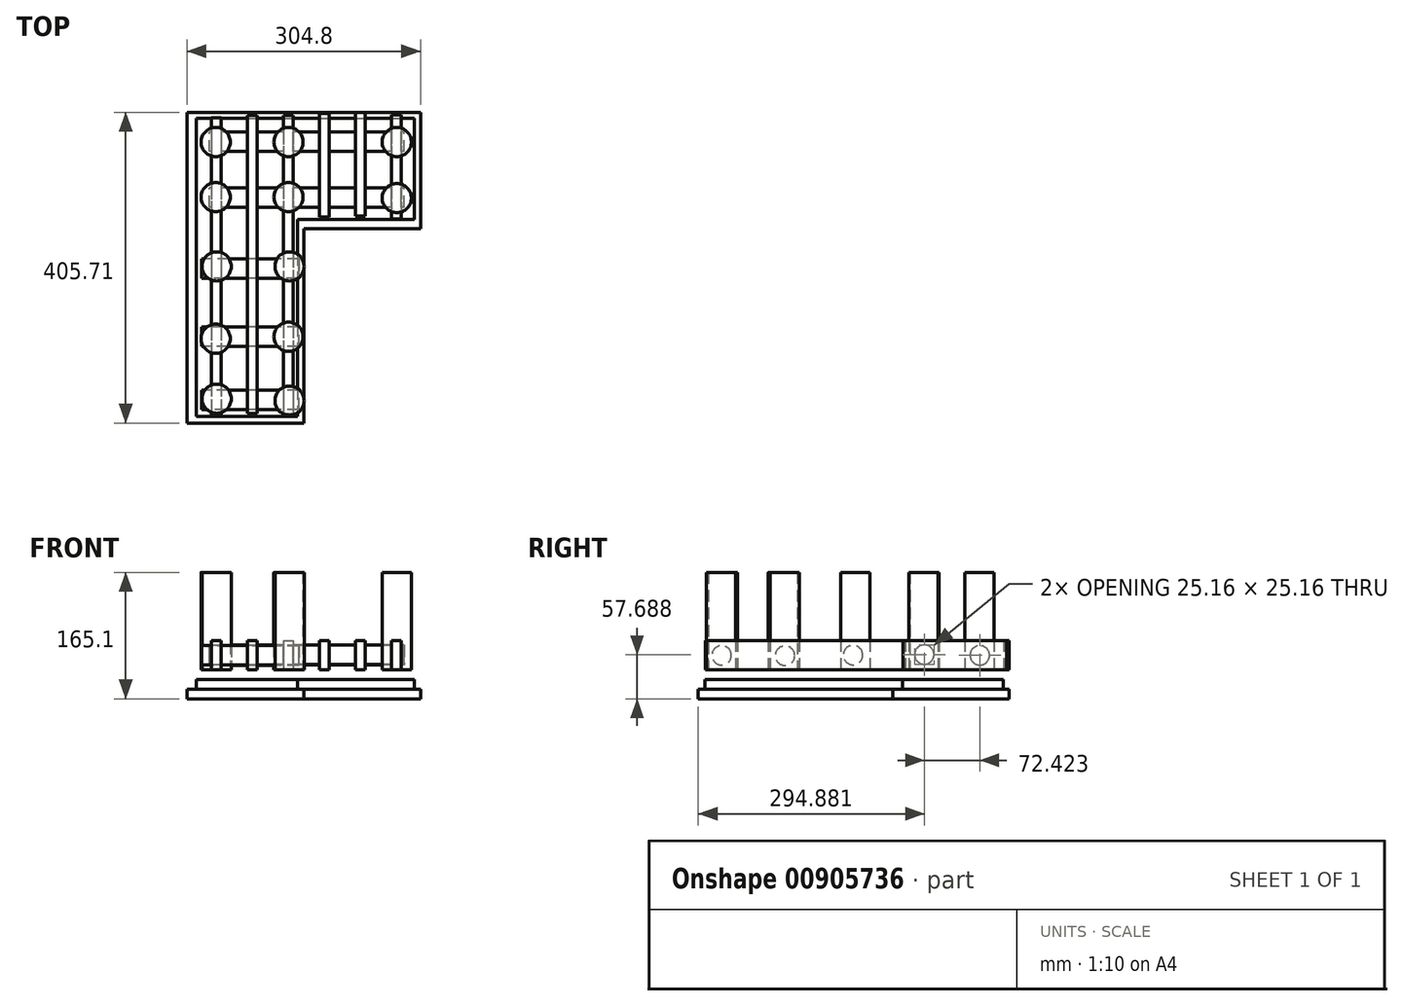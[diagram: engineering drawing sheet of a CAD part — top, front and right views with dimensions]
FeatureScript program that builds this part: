
annotation { "Feature Type Name" : "Feature", "Feature Type Description" : "" }
export const myFeature = defineFeature(function(context is Context, id is Id, definition is map)
    precondition{}
    {
        {
            var Q0;
            Q0=qCreatedBy(makeId("Top.planeOp"),FACE);
            var sketch = newSketch(context, id + "F0", { "sketchPlane" : qUnion([Q0])});
            skLineSegment(sketch, "E0.bottom", {"start": v(-152.4, 201.86) * mm, "end": v(152.4, 201.86) * mm});
            skLineSegment(sketch, "E0.top", {"start": v(-152.4, 201.06) * mm, "end": v(152.4, 201.06) * mm});
            skLineSegment(sketch, "E0.left", {"start": v(-152.4, 201.86) * mm, "end": v(-152.4, 201.06) * mm});
            skLineSegment(sketch, "E0.right", {"start": v(152.4, 201.86) * mm, "end": v(152.4, 201.06) * mm});
            skPoint(sketch, "E0.middle", {"position": v(0, 201.46) * mm});
            skLineSegment(sketch, "E1.bottom", {"start": v(-152.4, 201.86) * mm, "end": v(-152.4, 201.86) * mm});
            skLineSegment(sketch, "E1.top", {"start": v(-152.4, -204.54) * mm, "end": v(-152.4, -204.54) * mm});
            skLineSegment(sketch, "E1.left", {"start": v(-152.4, 201.86) * mm, "end": v(-152.4, -204.54) * mm});
            skLineSegment(sketch, "E1.right", {"start": v(-152.4, 201.86) * mm, "end": v(-152.4, -204.54) * mm});
            skLineSegment(sketch, "E2.bottom", {"start": v(-152.4, -204.54) * mm, "end": v(0, -204.54) * mm});
            skLineSegment(sketch, "E2.top", {"start": v(-152.4, -204.54) * mm, "end": v(0, -204.54) * mm});
            skLineSegment(sketch, "E2.right", {"start": v(0, -204.54) * mm, "end": v(0, -204.54) * mm});
            skLineSegment(sketch, "E3.top", {"start": v(0, 49.46) * mm, "end": v(0, 49.46) * mm});
            skLineSegment(sketch, "E3.left", {"start": v(0, -204.54) * mm, "end": v(0, 49.46) * mm});
            skLineSegment(sketch, "E3.right", {"start": v(0, -204.54) * mm, "end": v(0, 49.46) * mm});
            skLineSegment(sketch, "E4.bottom", {"start": v(0, 49.46) * mm, "end": v(152.4, 49.46) * mm});
            skLineSegment(sketch, "E4.top", {"start": v(0, 49.46) * mm, "end": v(152.4, 49.46) * mm});
            skLineSegment(sketch, "E4.right", {"start": v(152.4, 49.46) * mm, "end": v(152.4, 49.46) * mm});
            skLineSegment(sketch, "E5.bottom", {"start": v(152.4, 201.06) * mm, "end": v(152.4, 201.06) * mm});
            skLineSegment(sketch, "E5.left", {"start": v(152.4, 201.06) * mm, "end": v(152.4, 49.46) * mm});
            skLineSegment(sketch, "E5.right", {"start": v(152.4, 201.06) * mm, "end": v(152.4, 49.46) * mm});
            skSolve(sketch);
        }
        {
            var Q0;
            Q0=qCreatedBy(makeId("Top.planeOp"),FACE);
            var sketch = newSketch(context, id + "F1", { "sketchPlane" : qUnion([Q0])});
            skLineSegment(sketch, "E6.bottom", {"start": v(-148.7, 201.8) * mm, "end": v(-140.24, 201.8) * mm});
            skLineSegment(sketch, "E6.top", {"start": v(-148.7, -204.6) * mm, "end": v(-140.24, -204.6) * mm});
            skLineSegment(sketch, "E6.left", {"start": v(-148.7, 201.8) * mm, "end": v(-148.7, -204.6) * mm});
            skLineSegment(sketch, "E6.right", {"start": v(-140.24, 201.8) * mm, "end": v(-140.24, -204.6) * mm});
            skLineSegment(sketch, "E7.bottom", {"start": v(-140.24, 201.8) * mm, "end": v(156.1, 201.8) * mm});
            skLineSegment(sketch, "E7.top", {"start": v(-140.24, 193.33) * mm, "end": v(156.1, 193.33) * mm});
            skLineSegment(sketch, "E7.left", {"start": v(-140.24, 201.8) * mm, "end": v(-140.24, 193.33) * mm});
            skLineSegment(sketch, "E7.right", {"start": v(156.1, 201.8) * mm, "end": v(156.1, 193.33) * mm});
            skLineSegment(sketch, "E8.bottom", {"start": v(144.25, 193.33) * mm, "end": v(152.72, 193.33) * mm});
            skLineSegment(sketch, "E8.top", {"start": v(144.25, 49.4) * mm, "end": v(152.72, 49.4) * mm});
            skLineSegment(sketch, "E8.left", {"start": v(144.25, 193.33) * mm, "end": v(144.25, 49.4) * mm});
            skLineSegment(sketch, "E8.right", {"start": v(152.72, 193.33) * mm, "end": v(152.72, 49.4) * mm});
            skLineSegment(sketch, "E9.bottom", {"start": v(0, 53.12) * mm, "end": v(144.25, 53.12) * mm});
            skLineSegment(sketch, "E9.top", {"start": v(0, 61.58) * mm, "end": v(144.25, 61.58) * mm});
            skLineSegment(sketch, "E9.left", {"start": v(0, 53.12) * mm, "end": v(0, 61.58) * mm});
            skLineSegment(sketch, "E9.right", {"start": v(144.25, 53.12) * mm, "end": v(144.25, 61.58) * mm});
            skLineSegment(sketch, "E10.bottom", {"start": v(0, 61.58) * mm, "end": v(-8.47, 61.58) * mm});
            skLineSegment(sketch, "E10.top", {"start": v(0, -203.03) * mm, "end": v(-8.47, -203.03) * mm});
            skLineSegment(sketch, "E10.left", {"start": v(0, 61.58) * mm, "end": v(0, -203.03) * mm});
            skLineSegment(sketch, "E10.right", {"start": v(-8.47, 61.58) * mm, "end": v(-8.47, -203.03) * mm});
            skLineSegment(sketch, "E11.bottom", {"start": v(-140.24, -204.6) * mm, "end": v(-8.47, -204.6) * mm});
            skLineSegment(sketch, "E11.top", {"start": v(-140.24, -196.13) * mm, "end": v(-8.47, -196.13) * mm});
            skLineSegment(sketch, "E11.left", {"start": v(-140.24, -204.6) * mm, "end": v(-140.24, -196.13) * mm});
            skLineSegment(sketch, "E11.right", {"start": v(-8.47, -204.6) * mm, "end": v(-8.47, -196.13) * mm});
            skSolve(sketch);
        }
        {
            var Q0;
            Q0=makeQuery(id+"F0.imprint","IMPRINT",FACE,{"disambiguationData":[TD([[makeQuery(id+"F0.imprint","IMPRINT",EDGE,{"derivedFrom":sQuery(id+"F0.wireOp",EDGE,"E0.top")}),-1.0]])]});
            extrude(context, id + "F2", {"entities" : qUnion([Q0]), "depth" : 12.7 * mm, "offsetDistance" : 25.4 * mm});
        }
        {
            var Q0;
            {var subQ0=sQuery(id+"F1.wireOp",EDGE,"E9.top");Q0=makeQuery(id+"F1.imprint","IMPRINT",FACE,{"disambiguationData":[TD([[makeQuery(id+"F1.imprint","IMPRINT",EDGE,{"derivedFrom":subQ0}),1.0]])]});}
            extrude(context, id + "F3", {"entities" : qUnion([Q0]), "operationType" : NewBodyOperationType.ADD, "depth" : 25.4 * mm, "offsetDistance" : 25.4 * mm});
        }
        {
            var Q0;
            Q0=makeQuery(id+"F2.opExtrude","CAP_FACE",FACE,{"disambiguationData":[OSD([sQuery(id+"F0.wireOp",EDGE,"E0.top"),sQuery(id+"F0.wireOp",EDGE,"E1.left"),sQuery(id+"F0.wireOp",EDGE,"E2.bottom"),sQuery(id+"F0.wireOp",EDGE,"E3.left"),sQuery(id+"F0.wireOp",EDGE,"E4.bottom"),sQuery(id+"F0.wireOp",EDGE,"E5.left")])],"isStart":false});
            cPlane(context, id + "F4", {"entities" : qUnion([Q0]), "cplaneType" : CPlaneType.OFFSET, "offset" : 25.4 * mm, "width" : 152.4 * mm, "height" : 152.4 * mm});
        }
        {
            var Q0;
            Q0=qCreatedBy(id+"F4.planeOp",FACE);
            var sketch = newSketch(context, id + "F5", { "sketchPlane" : qUnion([Q0])});
            skLineSegment(sketch, "E12.bottom", {"start": v(-120.49, 194.07) * mm, "end": v(-107.79, 194.07) * mm});
            skLineSegment(sketch, "E12.top", {"start": v(-120.49, -195.4) * mm, "end": v(-107.79, -195.4) * mm});
            skLineSegment(sketch, "E12.left", {"start": v(-120.49, 194.07) * mm, "end": v(-120.49, -195.4) * mm});
            skLineSegment(sketch, "E12.right", {"start": v(-107.79, 194.07) * mm, "end": v(-107.79, -195.4) * mm});
            skLineSegment(sketch, "E13.bottom", {"start": v(-73.5, 197.5) * mm, "end": v(-60.8, 197.5) * mm});
            skLineSegment(sketch, "E13.top", {"start": v(-73.5, -191.97) * mm, "end": v(-60.8, -191.97) * mm});
            skLineSegment(sketch, "E13.left", {"start": v(-73.5, 197.5) * mm, "end": v(-73.5, -191.97) * mm});
            skLineSegment(sketch, "E13.right", {"start": v(-60.8, 197.5) * mm, "end": v(-60.8, -191.97) * mm});
            skLineSegment(sketch, "E14.bottom", {"start": v(-26.5, 197.3) * mm, "end": v(-13.8, 197.3) * mm});
            skLineSegment(sketch, "E14.top", {"start": v(-26.5, -192.18) * mm, "end": v(-13.8, -192.18) * mm});
            skLineSegment(sketch, "E14.left", {"start": v(-26.5, 197.3) * mm, "end": v(-26.5, -192.18) * mm});
            skLineSegment(sketch, "E14.right", {"start": v(-13.8, 197.3) * mm, "end": v(-13.8, -192.18) * mm});
            skLineSegment(sketch, "E15.bottom", {"start": v(20.48, 199.8) * mm, "end": v(33.18, 199.8) * mm});
            skLineSegment(sketch, "E15.top", {"start": v(20.48, 64.33) * mm, "end": v(33.18, 64.33) * mm});
            skLineSegment(sketch, "E15.left", {"start": v(20.48, 199.8) * mm, "end": v(20.48, 64.33) * mm});
            skLineSegment(sketch, "E15.right", {"start": v(33.18, 199.8) * mm, "end": v(33.18, 64.33) * mm});
            skLineSegment(sketch, "E16.bottom", {"start": v(67.47, 201.17) * mm, "end": v(80.17, 201.17) * mm});
            skLineSegment(sketch, "E16.top", {"start": v(67.47, 65.7) * mm, "end": v(80.17, 65.7) * mm});
            skLineSegment(sketch, "E16.left", {"start": v(67.47, 201.17) * mm, "end": v(67.47, 65.7) * mm});
            skLineSegment(sketch, "E16.right", {"start": v(80.17, 201.17) * mm, "end": v(80.17, 65.7) * mm});
            skLineSegment(sketch, "E17.bottom", {"start": v(114.46, 197.74) * mm, "end": v(127.16, 197.74) * mm});
            skLineSegment(sketch, "E17.top", {"start": v(114.46, 62.27) * mm, "end": v(127.16, 62.27) * mm});
            skLineSegment(sketch, "E17.left", {"start": v(114.46, 197.74) * mm, "end": v(114.46, 62.27) * mm});
            skLineSegment(sketch, "E17.right", {"start": v(127.16, 197.74) * mm, "end": v(127.16, 62.27) * mm});
            skLineSegment(sketch, "E18", {"start": v(-107.79, 27.82) * mm, "end": v(-73.5, 27.82) * mm});
            skLineSegment(sketch, "E19", {"start": v(-60.8, 127.66) * mm, "end": v(-26.5, 127.66) * mm});
            skLineSegment(sketch, "E20", {"start": v(-13.8, 169.3) * mm, "end": v(20.48, 169.3) * mm});
            skLineSegment(sketch, "E21", {"start": v(33.18, 132.06) * mm, "end": v(67.47, 132.06) * mm});
            skLineSegment(sketch, "E22", {"start": v(80.17, 154.03) * mm, "end": v(114.46, 154.03) * mm});
            skSolve(sketch);
        }
        {
            var Q0;
            Q0=makeQuery(id+"F5.imprint","IMPRINT",FACE,{"disambiguationData":[TD([[makeQuery(id+"F5.imprint","IMPRINT",EDGE,{"derivedFrom":sQuery(id+"F5.wireOp",EDGE,"E13.bottom")}),-1.0]])]});
            var Q1;
            Q1=makeQuery(id+"F5.imprint","IMPRINT",FACE,{"disambiguationData":[TD([[makeQuery(id+"F5.imprint","IMPRINT",EDGE,{"derivedFrom":sQuery(id+"F5.wireOp",EDGE,"E12.bottom")}),-1.0]])]});
            var Q2;
            Q2=makeQuery(id+"F5.imprint","IMPRINT",FACE,{"disambiguationData":[TD([[makeQuery(id+"F5.imprint","IMPRINT",EDGE,{"derivedFrom":sQuery(id+"F5.wireOp",EDGE,"E14.bottom")}),-1.0]])]});
            var Q3;
            Q3=makeQuery(id+"F5.imprint","IMPRINT",FACE,{"disambiguationData":[TD([[makeQuery(id+"F5.imprint","IMPRINT",EDGE,{"derivedFrom":sQuery(id+"F5.wireOp",EDGE,"E15.bottom")}),-1.0]])]});
            var Q4;
            Q4=makeQuery(id+"F5.imprint","IMPRINT",FACE,{"disambiguationData":[TD([[makeQuery(id+"F5.imprint","IMPRINT",EDGE,{"derivedFrom":sQuery(id+"F5.wireOp",EDGE,"E16.bottom")}),-1.0]])]});
            var Q5;
            Q5=makeQuery(id+"F5.imprint","IMPRINT",FACE,{"disambiguationData":[TD([[makeQuery(id+"F5.imprint","IMPRINT",EDGE,{"derivedFrom":sQuery(id+"F5.wireOp",EDGE,"E17.bottom")}),-1.0]])]});
            extrude(context, id + "F6", {"entities" : qUnion([Q0, Q1, Q2, Q3, Q4, Q5]), "depth" : 38.1 * mm, "offsetDistance" : 25.4 * mm});
        }
        {
            var Q0;
            Q0=makeQuery(id+"F6.opExtrude","SWEPT_FACE",FACE,{"disambiguationData":[OSD([sQuery(id+"F5.wireOp",EDGE,"E12.left")])]});
            var sketch = newSketch(context, id + "F7", { "sketchPlane" : qUnion([Q0])});
            skCircle(sketch, "E23", {"center": v(-162.64, 56.95) * mm, "radius": 12.7 * mm});
            skCircle(sketch, "E24", {"center": v(-90.22, 57.8) * mm, "radius": 12.7 * mm});
            skCircle(sketch, "E25", {"center": v(2.88, 57.24) * mm, "radius": 12.7 * mm});
            skCircle(sketch, "E26", {"center": v(91.52, 56.39) * mm, "radius": 12.7 * mm});
            skCircle(sketch, "E27", {"center": v(174.14, 56.95) * mm, "radius": 12.7 * mm});
            skSolve(sketch);
        }
        {
            var Q0;
            Q0=makeQuery(id+"F7.imprint","IMPRINT",FACE,{"disambiguationData":[TD([[makeQuery(id+"F7.imprint","IMPRINT",EDGE,{"derivedFrom":sQuery(id+"F7.wireOp",EDGE,"E24")}),1.0]])]});
            var Q1;
            Q1=makeQuery(id+"F7.imprint","IMPRINT",FACE,{"disambiguationData":[TD([[makeQuery(id+"F7.imprint","IMPRINT",EDGE,{"derivedFrom":sQuery(id+"F7.wireOp",EDGE,"E23")}),1.0]])]});
            extrude(context, id + "F8", {"entities" : qUnion([Q0, Q1]), "operationType" : NewBodyOperationType.ADD, "oppositeDirection" : true, "depth" : 251.46 * mm, "offsetDistance" : 25.4 * mm, "hasSecondDirection" : true, "secondDirectionOppositeDirection" : false, "secondDirectionDepth" : 2.54 * mm});
        }
        {
            var Q0;
            Q0=makeQuery(id+"F7.imprint","IMPRINT",FACE,{"disambiguationData":[TD([[makeQuery(id+"F7.imprint","IMPRINT",EDGE,{"derivedFrom":sQuery(id+"F7.wireOp",EDGE,"E27")}),1.0]])]});
            var Q1;
            Q1=makeQuery(id+"F7.imprint","IMPRINT",FACE,{"disambiguationData":[TD([[makeQuery(id+"F7.imprint","IMPRINT",EDGE,{"derivedFrom":sQuery(id+"F7.wireOp",EDGE,"E25")}),1.0]])]});
            var Q2;
            Q2=makeQuery(id+"F7.imprint","IMPRINT",FACE,{"disambiguationData":[TD([[makeQuery(id+"F7.imprint","IMPRINT",EDGE,{"derivedFrom":sQuery(id+"F7.wireOp",EDGE,"E26")}),1.0]])]});
            extrude(context, id + "F9", {"entities" : qUnion([Q0, Q1, Q2]), "oppositeDirection" : true, "depth" : 114.3 * mm, "offsetDistance" : 25.4 * mm, "hasSecondDirection" : true, "secondDirectionOppositeDirection" : false, "secondDirectionDepth" : 12.7 * mm});
        }
        {
            var Q0;
            Q0=qCreatedBy(id+"F4.planeOp",FACE);
            var sketch = newSketch(context, id + "F10", { "sketchPlane" : qUnion([Q0])});
            skCircle(sketch, "E28", {"center": v(-114.92, 162.44) * mm, "radius": 19.05 * mm});
            skCircle(sketch, "E29", {"center": v(121.34, 162.44) * mm, "radius": 19.05 * mm});
            skCircle(sketch, "E30", {"center": v(-114.92, 90.53) * mm, "radius": 19.05 * mm});
            skCircle(sketch, "E31", {"center": v(121.34, 89.24) * mm, "radius": 19.05 * mm});
            skCircle(sketch, "E32", {"center": v(-113.64, 0) * mm, "radius": 19.05 * mm});
            skCircle(sketch, "E33", {"center": v(-18.62, 0) * mm, "radius": 19.05 * mm});
            skCircle(sketch, "E34", {"center": v(-114.92, -94.38) * mm, "radius": 19.05 * mm});
            skCircle(sketch, "E35", {"center": v(-19.9, -91.8) * mm, "radius": 19.05 * mm});
            skCircle(sketch, "E36", {"center": v(-113.64, -172.7) * mm, "radius": 19.05 * mm});
            skCircle(sketch, "E37", {"center": v(-18.62, -175.27) * mm, "radius": 19.05 * mm});
            skCircle(sketch, "E38", {"center": v(-19.9, 90.53) * mm, "radius": 19.05 * mm});
            skCircle(sketch, "E39", {"center": v(-19.9, 162.44) * mm, "radius": 19.05 * mm});
            skSolve(sketch);
        }
        {
            var Q0;
            Q0=makeQuery(id+"F10.imprint","IMPRINT",FACE,{"disambiguationData":[TD([[makeQuery(id+"F10.imprint","IMPRINT",EDGE,{"derivedFrom":sQuery(id+"F10.wireOp",EDGE,"E36")}),1.0]])]});
            var Q1;
            Q1=makeQuery(id+"F10.imprint","IMPRINT",FACE,{"disambiguationData":[TD([[makeQuery(id+"F10.imprint","IMPRINT",EDGE,{"derivedFrom":sQuery(id+"F10.wireOp",EDGE,"E34")}),1.0]])]});
            var Q2;
            Q2=makeQuery(id+"F10.imprint","IMPRINT",FACE,{"disambiguationData":[TD([[makeQuery(id+"F10.imprint","IMPRINT",EDGE,{"derivedFrom":sQuery(id+"F10.wireOp",EDGE,"E37")}),1.0]])]});
            var Q3;
            Q3=makeQuery(id+"F10.imprint","IMPRINT",FACE,{"disambiguationData":[TD([[makeQuery(id+"F10.imprint","IMPRINT",EDGE,{"derivedFrom":sQuery(id+"F10.wireOp",EDGE,"E35")}),1.0]])]});
            var Q4;
            Q4=makeQuery(id+"F10.imprint","IMPRINT",FACE,{"disambiguationData":[TD([[makeQuery(id+"F10.imprint","IMPRINT",EDGE,{"derivedFrom":sQuery(id+"F10.wireOp",EDGE,"E33")}),1.0]])]});
            var Q5;
            Q5=makeQuery(id+"F10.imprint","IMPRINT",FACE,{"disambiguationData":[TD([[makeQuery(id+"F10.imprint","IMPRINT",EDGE,{"derivedFrom":sQuery(id+"F10.wireOp",EDGE,"E32")}),1.0]])]});
            var Q6;
            Q6=makeQuery(id+"F10.imprint","IMPRINT",FACE,{"disambiguationData":[TD([[makeQuery(id+"F10.imprint","IMPRINT",EDGE,{"derivedFrom":sQuery(id+"F10.wireOp",EDGE,"E30")}),1.0]])]});
            var Q7;
            Q7=makeQuery(id+"F10.imprint","IMPRINT",FACE,{"disambiguationData":[TD([[makeQuery(id+"F10.imprint","IMPRINT",EDGE,{"derivedFrom":sQuery(id+"F10.wireOp",EDGE,"E28")}),1.0]])]});
            var Q8;
            Q8=makeQuery(id+"F10.imprint","IMPRINT",FACE,{"disambiguationData":[TD([[makeQuery(id+"F10.imprint","IMPRINT",EDGE,{"derivedFrom":sQuery(id+"F10.wireOp",EDGE,"E39")}),1.0]])]});
            var Q9;
            Q9=makeQuery(id+"F10.imprint","IMPRINT",FACE,{"disambiguationData":[TD([[makeQuery(id+"F10.imprint","IMPRINT",EDGE,{"derivedFrom":sQuery(id+"F10.wireOp",EDGE,"E38")}),1.0]])]});
            var Q10;
            Q10=makeQuery(id+"F10.imprint","IMPRINT",FACE,{"disambiguationData":[TD([[makeQuery(id+"F10.imprint","IMPRINT",EDGE,{"derivedFrom":sQuery(id+"F10.wireOp",EDGE,"E31")}),1.0]])]});
            var Q11;
            Q11=makeQuery(id+"F10.imprint","IMPRINT",FACE,{"disambiguationData":[TD([[makeQuery(id+"F10.imprint","IMPRINT",EDGE,{"derivedFrom":sQuery(id+"F10.wireOp",EDGE,"E29")}),1.0]])]});
            extrude(context, id + "F11", {"entities" : qUnion([Q0, Q1, Q2, Q3, Q4, Q5, Q6, Q7, Q8, Q9, Q10, Q11]), "depth" : 127 * mm, "offsetDistance" : 25.4 * mm});
        }
    });
